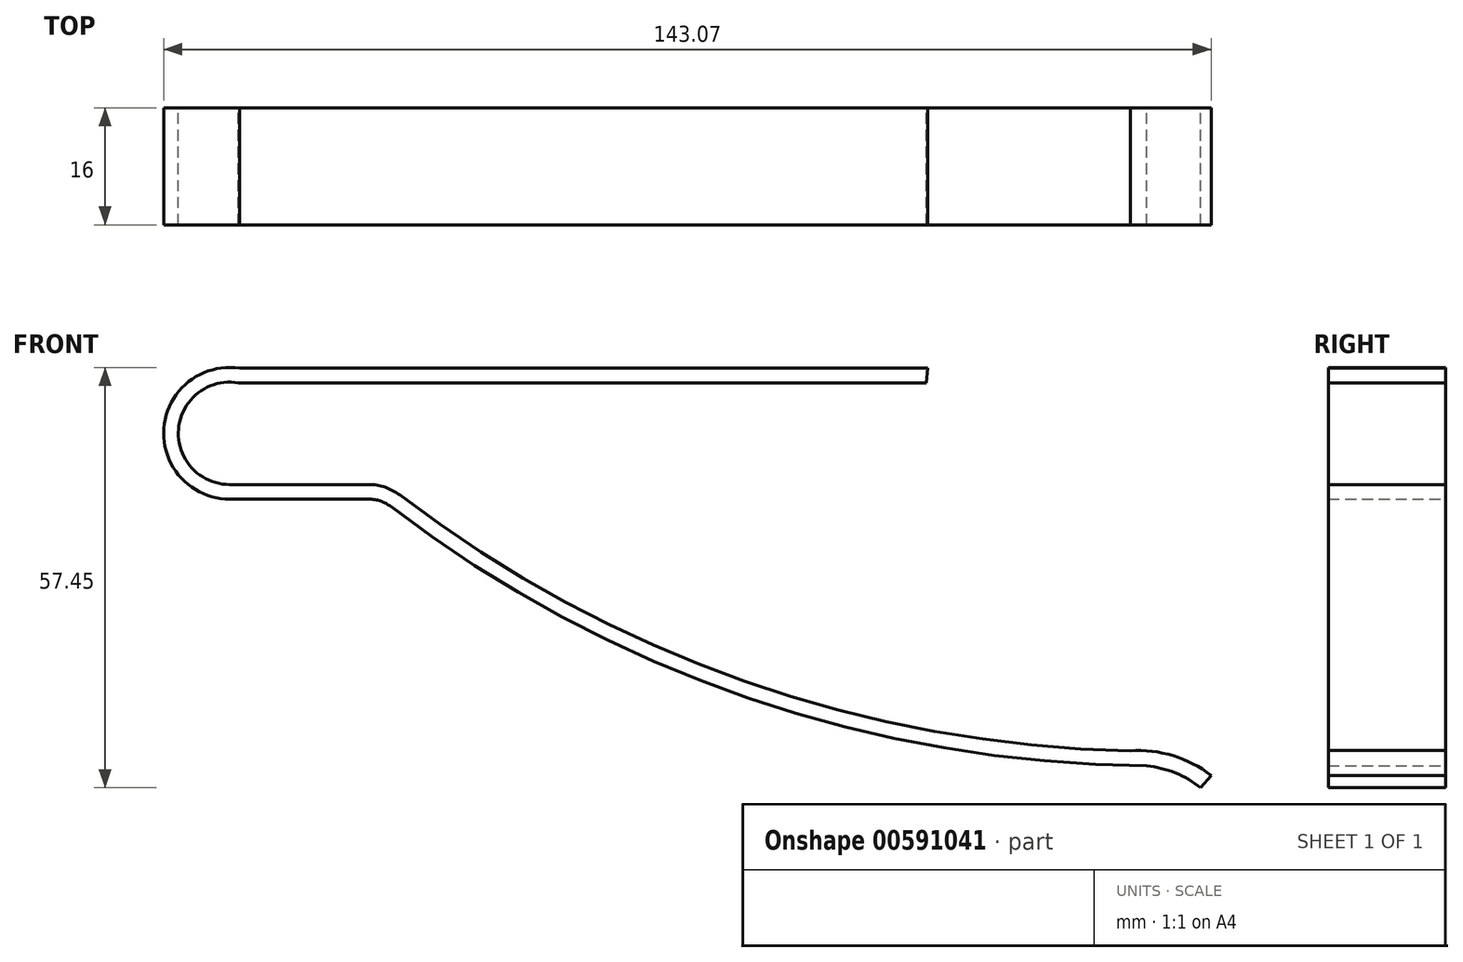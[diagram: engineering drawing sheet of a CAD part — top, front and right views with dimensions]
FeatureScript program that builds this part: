
annotation { "Feature Type Name" : "Feature", "Feature Type Description" : "" }
export const myFeature = defineFeature(function(context is Context, id is Id, definition is map)
    precondition{}
    {
        {
            var Q0;
            Q0=qCreatedBy(makeId("Front.planeOp"),FACE);
            var sketch = newSketch(context, id + "F0", { "sketchPlane" : qUnion([Q0])});
            skArc(sketch, "E0", {"start": v(1.34, 8.9) * mm, "mid": v(-8.97, 0.67) * mm, "end": v(0, -9) * mm});
            skLineSegment(sketch, "E1", {"start": v(1.34, 8.9) * mm, "end": v(95.34, 8.9) * mm});
            skLineSegment(sketch, "E2", {"start": v(0, -9) * mm, "end": v(19, -9) * mm});
            skArc(sketch, "E3", {"start": v(22.04, -10.03) * mm, "mid": v(70.76, -36.14) * mm, "end": v(125.25, -45.45) * mm});
            skPoint(sketch, "E4.visualSharp", {"position": v(20.7, -9) * mm});
            skArc(sketch, "E4.filletArc", {"start": v(22.04, -10.03) * mm, "mid": v(20.6, -9.26) * mm, "end": v(19, -9) * mm});
            skLineSegment(sketch, "E5.0", {"start": v(1.18, 6.9) * mm, "end": v(95.18, 6.9) * mm});
            skArc(sketch, "E5.1", {"start": v(1.18, 6.9) * mm, "mid": v(-6.97, 0.6) * mm, "end": v(0, -7) * mm});
            skArc(sketch, "E5.3", {"start": v(23.25, -8.44) * mm, "mid": v(70.35, -33.88) * mm, "end": v(123.01, -43.41) * mm});
            skArc(sketch, "E5.4", {"start": v(23.25, -8.44) * mm, "mid": v(21.25, -7.37) * mm, "end": v(19, -7) * mm});
            skLineSegment(sketch, "E5.5", {"start": v(0, -7) * mm, "end": v(19, -7) * mm});
            skArc(sketch, "E6", {"start": v(132.62, -48.45) * mm, "mid": v(129.15, -46.42) * mm, "end": v(125.25, -45.45) * mm});
            skLineSegment(sketch, "E7", {"start": v(95.34, 8.9) * mm, "end": v(95.18, 6.9) * mm});
            skArc(sketch, "E8", {"start": v(134.07, -46.77) * mm, "mid": v(128.85, -44.06) * mm, "end": v(123.01, -43.41) * mm});
            skLineSegment(sketch, "E9", {"start": v(134.07, -46.77) * mm, "end": v(132.62, -48.45) * mm});
            skSolve(sketch);
        }
        {
            var Q0;
            Q0 = qSketchRegion(id + "F0", true);
            extrude(context, id + "F1", {"entities" : qUnion([Q0]), "depth" : 16 * mm, "offsetDistance" : 25 * mm});
        }
    });
